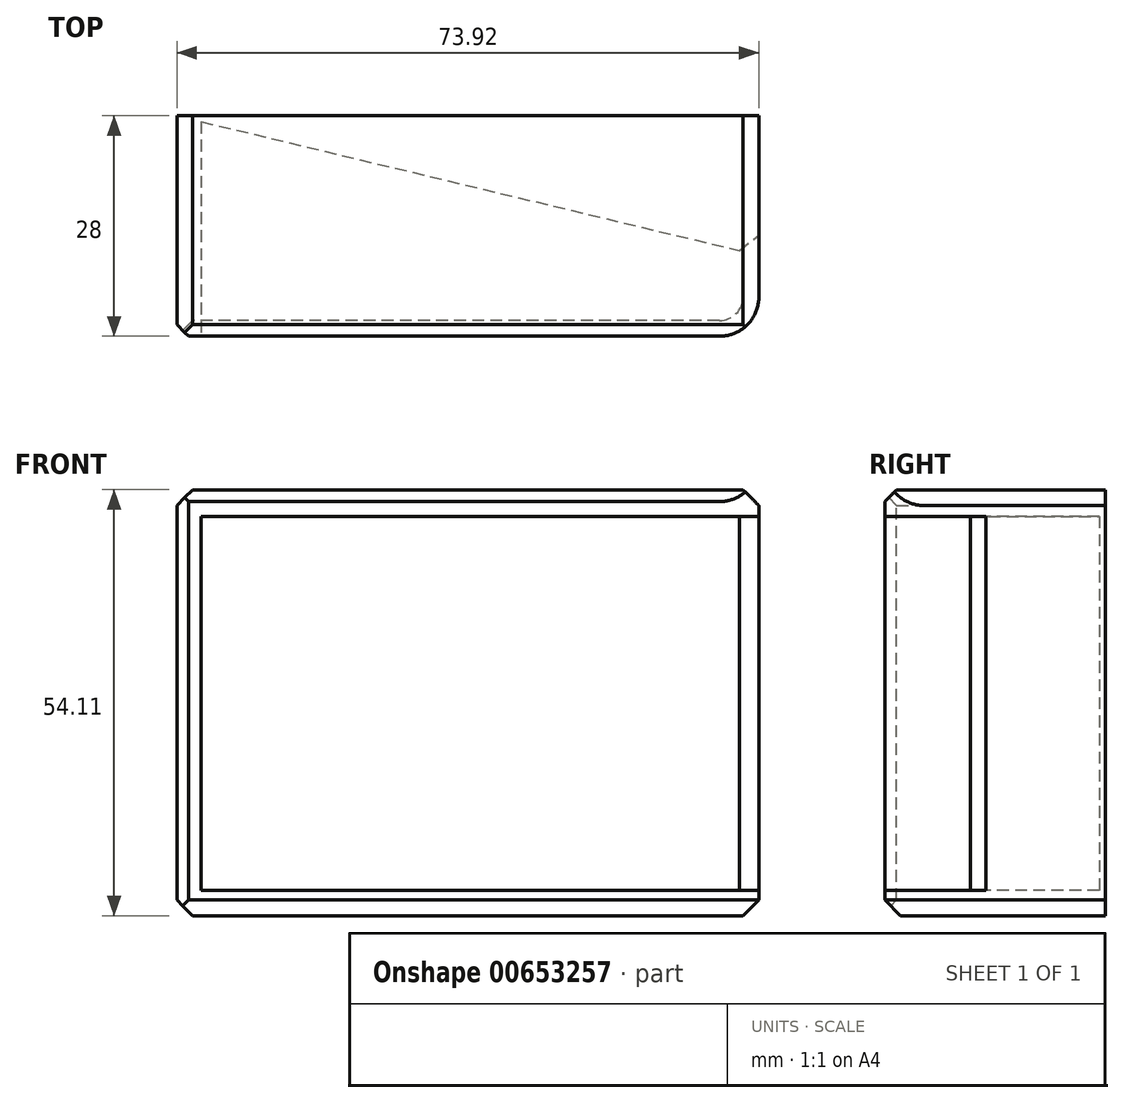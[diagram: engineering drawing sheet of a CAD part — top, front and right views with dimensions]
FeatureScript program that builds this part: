
annotation { "Feature Type Name" : "Feature", "Feature Type Description" : "" }
export const myFeature = defineFeature(function(context is Context, id is Id, definition is map)
    precondition{}
    {
        {
            var Q0;
            Q0=qCreatedBy(makeId("Front.planeOp"),FACE);
            var sketch = newSketch(context, id + "F0", { "sketchPlane" : qUnion([Q0])});
            skLineSegment(sketch, "E0", {"start": v(31.06, 0) * mm, "end": v(-42.86, 0) * mm});
            skLineSegment(sketch, "E1", {"start": v(-42.86, 0) * mm, "end": v(-42.86, 54.1) * mm});
            skLineSegment(sketch, "E2", {"start": v(-42.86, 54.1) * mm, "end": v(31.06, 54.1) * mm});
            skLineSegment(sketch, "E3", {"start": v(31.06, 54.1) * mm, "end": v(31.06, 50.73) * mm});
            skLineSegment(sketch, "E4", {"start": v(31.06, 50.73) * mm, "end": v(-39.77, 50.73) * mm});
            skLineSegment(sketch, "E5", {"start": v(-39.77, 50.73) * mm, "end": v(-39.77, 3.23) * mm});
            skLineSegment(sketch, "E6", {"start": v(-39.77, 3.23) * mm, "end": v(31.06, 3.23) * mm});
            skLineSegment(sketch, "E7", {"start": v(31.06, 3.23) * mm, "end": v(31.06, 0) * mm});
            skSolve(sketch);
        }
        {
            var Q0;
            Q0=qSketchRegion(id+"F0",true);
            extrude(context, id + "F1", {"entities" : qUnion([Q0]), "oppositeDirection" : true, "depth" : 28 * mm, "offsetDistance" : 25 * mm});
        }
        {
            var Q0;
            Q0=makeQuery(id+"F1.opExtrude","SWEPT_FACE",FACE,{"disambiguationData":[OSD([sQuery(id+"F0.wireOp",EDGE,"E0")])]});
            var sketch = newSketch(context, id + "F2", { "sketchPlane" : qUnion([Q0])});
            skLineSegment(sketch, "E8", {"start": v(-42.86, -28) * mm, "end": v(31.06, -10.29) * mm});
            skLineSegment(sketch, "E9", {"start": v(31.06, -10.29) * mm, "end": v(31.06, -28) * mm});
            skLineSegment(sketch, "E10", {"start": v(31.06, -28) * mm, "end": v(-42.86, -28) * mm});
            skSolve(sketch);
        }
        {
            var Q0;
            Q0=makeQuery(id+"F2.imprint","IMPRINT",FACE,{"disambiguationData":[TD([[makeQuery(id+"F2.imprint","IMPRINT",EDGE,{"derivedFrom":sQuery(id+"F2.wireOp",EDGE,"E8")}),-1.0]])]});
            extrude(context, id + "F3", {"entities" : qUnion([Q0]), "operationType" : NewBodyOperationType.ADD, "oppositeDirection" : true, "depth" : 54 * mm, "offsetDistance" : 25 * mm});
        }
        {
            var Q0;
            Q0=makeQuery(id+"F1.opExtrude","CAP_EDGE",EDGE,{"disambiguationData":[OSD([sQuery(id+"F0.wireOp",EDGE,"E0")])],"isStart":true});
            var Q1;
            Q1=makeQuery(id+"F1.opExtrude","CAP_EDGE",EDGE,{"disambiguationData":[OSD([sQuery(id+"F0.wireOp",EDGE,"E1")])],"isStart":true});
            var Q2;
            Q2=makeQuery(id+"F1.opExtrude","CAP_EDGE",EDGE,{"disambiguationData":[OSD([sQuery(id+"F0.wireOp",EDGE,"E2")])],"isStart":true});
            chamfer(context, id + "F4", {"entities" : qUnion([Q0, Q1, Q2]), "width" : 1.5 * mm, "tangentPropagation" : true});
        }
        {
            var Q0;
            Q0=makeQuery(id+"F1.opExtrude","CAP_EDGE",EDGE,{"disambiguationData":[OSD([sQuery(id+"F0.wireOp",EDGE,"E3")])],"isStart":true});
            var Q1;
            Q1=makeQuery(id+"F1.opExtrude","CAP_EDGE",EDGE,{"disambiguationData":[OSD([sQuery(id+"F0.wireOp",EDGE,"E7")])],"isStart":true});
            fillet(context, id + "F5", {"entities" : qUnion([Q0, Q1]), "radius" : 5 * mm, "tangentPropagation" : true, "allowEdgeOverflow" : false});
        }
        {
            var Q0;
            Q0=makeQuery(id+"F3.opExtrude","SWEPT_EDGE",EDGE,{"disambiguationData":[OSD([sQuery(id+"F0.wireOp",EDGE,"E0"),sQuery(id+"F0.wireOp",EDGE,"E7"),sQuery(id+"F2.wireOp",EDGE,"E8"),sQuery(id+"F2.wireOp",EDGE,"E9")])]});
            chamfer(context, id + "F6", {"entities" : qUnion([Q0]), "width" : 2 * mm, "tangentPropagation" : true});
        }
        {
            var Q0;
            Q0=makeQuery(id+"F1.opExtrude","SWEPT_EDGE",EDGE,{"disambiguationData":[OSD([sQuery(id+"F0.wireOp",EDGE,"E0"),sQuery(id+"F0.wireOp",EDGE,"E1")])]});
            var Q1;
            Q1=makeQuery(id+"F1.opExtrude","SWEPT_EDGE",EDGE,{"disambiguationData":[OSD([sQuery(id+"F0.wireOp",EDGE,"E1"),sQuery(id+"F0.wireOp",EDGE,"E2")])]});
            chamfer(context, id + "F7", {"entities" : qUnion([Q0, Q1]), "width" : 2 * mm, "tangentPropagation" : true});
        }
        {
            var Q0;
            Q0=makeQuery(id+"F1.opExtrude","SWEPT_EDGE",EDGE,{"disambiguationData":[OSD([sQuery(id+"F0.wireOp",EDGE,"E2"),sQuery(id+"F0.wireOp",EDGE,"E3")])]});
            var Q1;
            Q1=makeQuery(id+"F1.opExtrude","SWEPT_EDGE",EDGE,{"disambiguationData":[OSD([sQuery(id+"F0.wireOp",EDGE,"E0"),sQuery(id+"F0.wireOp",EDGE,"E7")])]});
            chamfer(context, id + "F8", {"entities" : qUnion([Q0, Q1]), "width" : 2 * mm, "tangentPropagation" : true});
        }
    });
